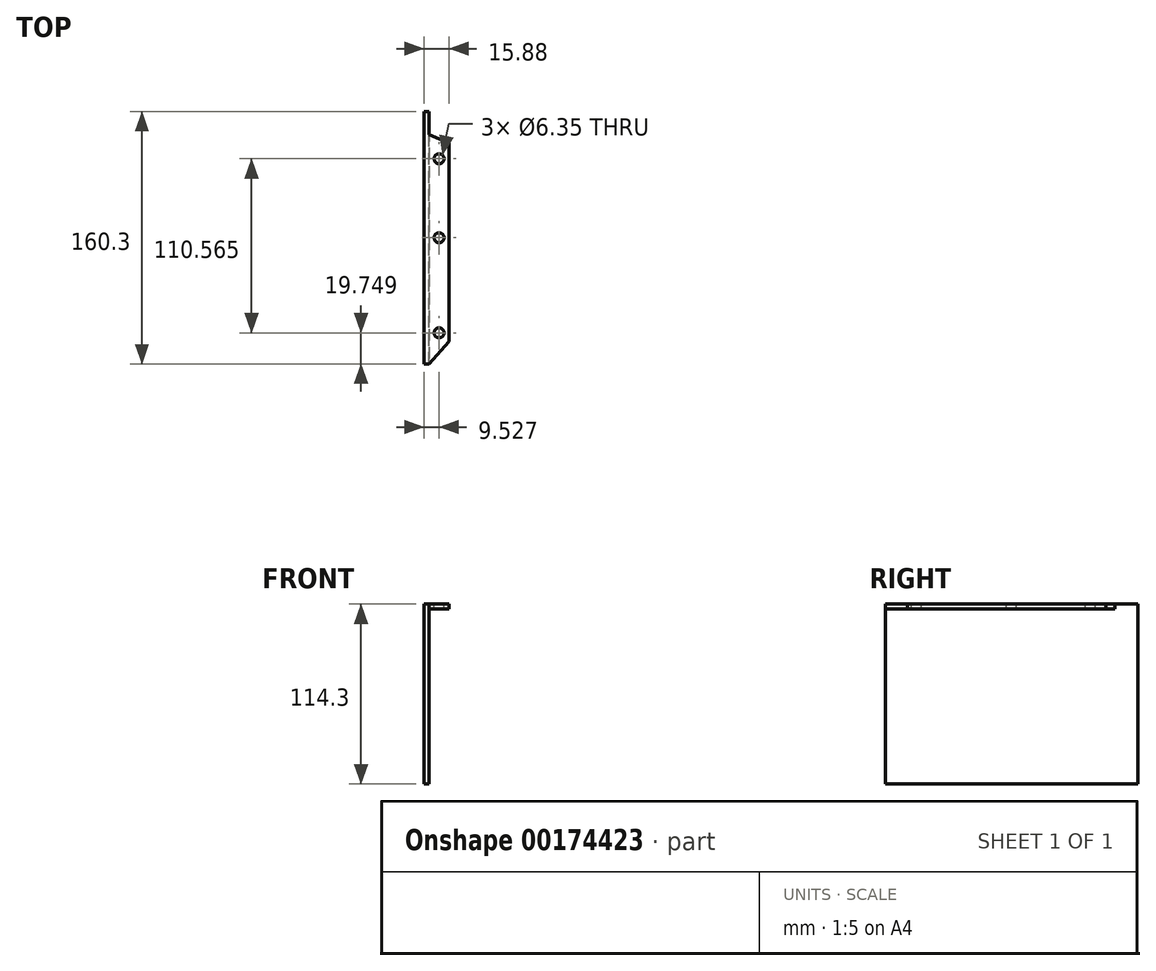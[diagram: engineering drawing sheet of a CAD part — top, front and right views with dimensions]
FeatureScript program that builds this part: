
annotation { "Feature Type Name" : "Feature", "Feature Type Description" : "" }
export const myFeature = defineFeature(function(context is Context, id is Id, definition is map)
    precondition{}
    {
        {
            var Q0;
            Q0=qCreatedBy(makeId("Top.planeOp"),FACE);
            var sketch = newSketch(context, id + "F0", { "sketchPlane" : qUnion([Q0])});
            skLineSegment(sketch, "E0.bottom", {"start": v(1.59, 80.15) * mm, "end": v(-1.59, 80.15) * mm});
            skLineSegment(sketch, "E0.top", {"start": v(1.59, -80.15) * mm, "end": v(-1.59, -80.15) * mm});
            skLineSegment(sketch, "E0.left", {"start": v(1.59, 80.15) * mm, "end": v(1.59, -80.15) * mm});
            skLineSegment(sketch, "E0.right", {"start": v(-1.59, 80.15) * mm, "end": v(-1.59, -80.15) * mm});
            skPoint(sketch, "E0.middle", {"position": v(0, 0) * mm});
            skLineSegment(sketch, "E1", {"start": v(-1.59, 80.15) * mm, "end": v(-1.59, 80.15) * mm});
            skLineSegment(sketch, "E2", {"start": v(-1.59, 80.15) * mm, "end": v(1.59, 80.15) * mm});
            skSolve(sketch);
        }
        {
            var Q0;
            Q0 = qSketchRegion(id + "F0", true);
            extrude(context, id + "F1", {"entities" : qUnion([Q0]), "depth" : 114.3 * mm});
        }
        {
            var Q0;
            Q0=makeQuery(id+"F1.opExtrude","SWEPT_FACE",FACE,{"disambiguationData":[OSD([sQuery(id+"F0.wireOp",EDGE,"E0.left")])]});
            var sketch = newSketch(context, id + "F2", { "sketchPlane" : qUnion([Q0])});
            skPoint(sketch, "E3", {"position": v(65.66, 114.3) * mm});
            skPoint(sketch, "E4", {"position": v(-80.15, 114.3) * mm});
            skLineSegment(sketch, "E5.bottom", {"start": v(-80.15, 114.3) * mm, "end": v(65.66, 114.3) * mm});
            skLineSegment(sketch, "E5.top", {"start": v(-80.15, 111.13) * mm, "end": v(65.66, 111.13) * mm});
            skLineSegment(sketch, "E5.left", {"start": v(-80.15, 114.3) * mm, "end": v(-80.15, 111.13) * mm});
            skLineSegment(sketch, "E5.right", {"start": v(65.66, 114.3) * mm, "end": v(65.66, 111.13) * mm});
            skSolve(sketch);
        }
        {
            var Q0;
            Q0 = qSketchRegion(id + "F2", true);
            extrude(context, id + "F3", {"entities" : qUnion([Q0]), "operationType" : NewBodyOperationType.ADD, "depth" : 12.7 * mm, "offsetDistance" : 25.4 * mm});
        }
        {
            var Q0;
            Q0=makeQuery(id+"F3.boolean.opBoolean","MERGE",FACE,{"derivedFrom":[makeQuery(id+"F1.opExtrude","CAP_FACE",FACE,{"disambiguationData":[OSD([sQuery(id+"F0.wireOp",EDGE,"E0.top"),sQuery(id+"F0.wireOp",EDGE,"E0.left"),sQuery(id+"F0.wireOp",EDGE,"E0.right"),sQuery(id+"F0.wireOp",EDGE,"E2")])],"isStart":false}),makeQuery(id+"F3.opExtrude","SWEPT_FACE",FACE,{"disambiguationData":[OSD([sQuery(id+"F2.wireOp",EDGE,"E5.bottom")])]})]});
            var sketch = newSketch(context, id + "F4", { "sketchPlane" : qUnion([Q0])});
            skLineSegment(sketch, "E6", {"start": v(1.59, 65.66) * mm, "end": v(14.29, 60.06) * mm});
            skLineSegment(sketch, "E7", {"start": v(14.29, 60.06) * mm, "end": v(14.29, 65.66) * mm});
            skLineSegment(sketch, "E8", {"start": v(14.29, 65.66) * mm, "end": v(1.59, 65.66) * mm});
            skLineSegment(sketch, "E9", {"start": v(14.29, -80.15) * mm, "end": v(1.59, -80.15) * mm});
            skPoint(sketch, "E9.endSnap0", {"position": v(6.35, -80.15) * mm});
            skLineSegment(sketch, "E10", {"start": v(1.59, -80.15) * mm, "end": v(14.29, -66.05) * mm});
            skLineSegment(sketch, "E11", {"start": v(14.29, -66.05) * mm, "end": v(14.29, -80.15) * mm});
            skSolve(sketch);
        }
        {
            var Q0;
            Q0 = qSketchRegion(id + "F4", true);
            extrude(context, id + "F5", {"entities" : qUnion([Q0]), "operationType" : NewBodyOperationType.REMOVE, "oppositeDirection" : true, "depth" : 25.4 * mm, "offsetDistance" : 25.4 * mm});
        }
        {
            var Q0;
            Q0=makeQuery(id+"F3.boolean.opBoolean","MERGE",FACE,{"derivedFrom":[makeQuery(id+"F1.opExtrude","CAP_FACE",FACE,{"disambiguationData":[OSD([sQuery(id+"F0.wireOp",EDGE,"E0.top"),sQuery(id+"F0.wireOp",EDGE,"E0.left"),sQuery(id+"F0.wireOp",EDGE,"E0.right"),sQuery(id+"F0.wireOp",EDGE,"E2")])],"isStart":false}),makeQuery(id+"F3.opExtrude","SWEPT_FACE",FACE,{"disambiguationData":[OSD([sQuery(id+"F2.wireOp",EDGE,"E5.bottom")])]})]});
            var sketch = newSketch(context, id + "F6", { "sketchPlane" : qUnion([Q0])});
            skLineSegment(sketch, "E12", {"start": v(7.94, 62.86) * mm, "end": v(7.94, -73.1) * mm});
            skCircle(sketch, "E13", {"center": v(7.94, 0) * mm, "radius": 3.18 * mm});
            skCircle(sketch, "E14", {"center": v(7.94, 50.16) * mm, "radius": 3.18 * mm});
            skCircle(sketch, "E15", {"center": v(7.94, -60.4) * mm, "radius": 3.18 * mm});
            skSolve(sketch);
        }
        {
            var Q0;
            Q0 = qSketchRegion(id + "F6", true);
            extrude(context, id + "F7", {"entities" : qUnion([Q0]), "operationType" : NewBodyOperationType.REMOVE, "oppositeDirection" : true, "depth" : 25.4 * mm, "offsetDistance" : 25.4 * mm});
        }
    });
